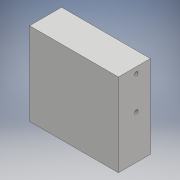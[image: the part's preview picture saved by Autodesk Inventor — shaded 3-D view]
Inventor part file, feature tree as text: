
AUTODESK INVENTOR PART (.ipt)
format: ipt  version: 2018 (Build 220112000, 112)  size: 100,864 bytes
history: native  units: mm
features: extrude x2, sketch x2
ambient origin geometry x8: Origin, YZ Plane, XZ Plane, XY Plane, X Axis, Y Axis, Z Axis, Center Point
bodies: Solid1 (feature_tree)
feature tree (4):
  extrude  "Extrusion1"  Depth=70.0mm
  extrude  "Extrusion2"  Depth=3.0mm
  sketch  "Sketch1"  dims[d1=75.0mm d2=70.0mm]
  sketch  "Sketch2"  dims[d3=27.0mm d4=0.0mm d5=3.0mm d6=12.0mm d7=5.0mm d8=3.0mm d9=28.0mm d10=3.0mm d11=0.0mm]
